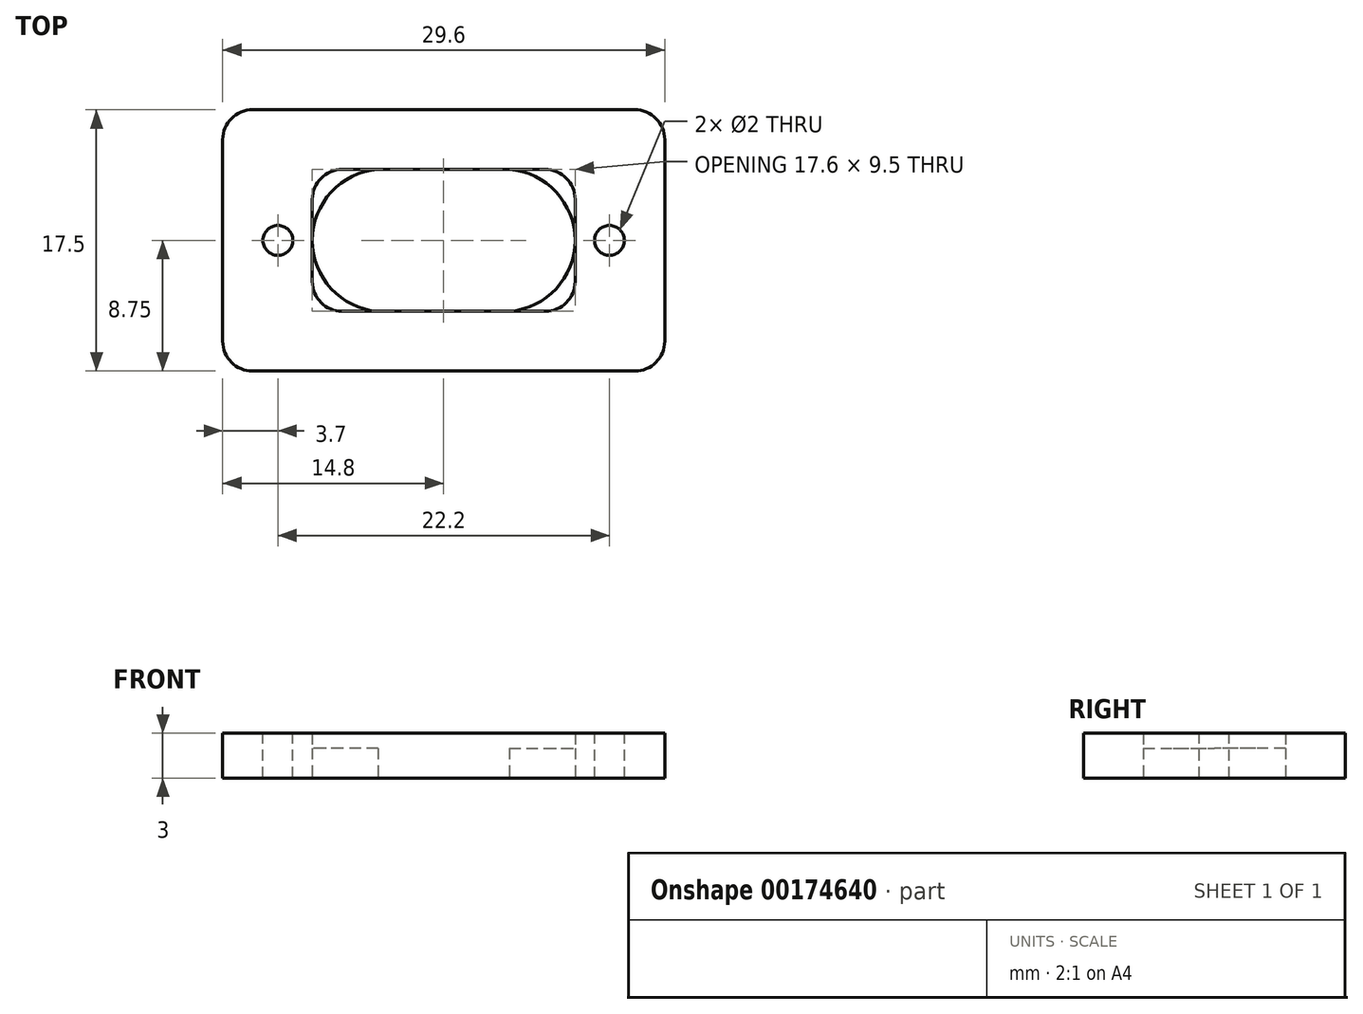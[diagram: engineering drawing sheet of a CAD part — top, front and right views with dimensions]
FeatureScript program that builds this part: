
annotation { "Feature Type Name" : "Feature", "Feature Type Description" : "" }
export const myFeature = defineFeature(function(context is Context, id is Id, definition is map)
    precondition{}
    {
        {
            var Q0;
            Q0=qCreatedBy(makeId("Top.planeOp"),FACE);
            var sketch = newSketch(context, id + "F0", { "sketchPlane" : qUnion([Q0])});
            skLineSegment(sketch, "E0", {"start": v(0, 4.75) * mm, "end": v(-8.8, 4.75) * mm});
            skLineSegment(sketch, "E1", {"start": v(-8.8, 4.75) * mm, "end": v(-8.8, 0) * mm});
            skLineSegment(sketch, "E2", {"start": v(-8.8, 0) * mm, "end": v(0, 0) * mm});
            skLineSegment(sketch, "E3", {"start": v(0, 0) * mm, "end": v(0, 4.75) * mm});
            skLineSegment(sketch, "E4", {"start": v(0, 4.75) * mm, "end": v(0, 8.75) * mm});
            skLineSegment(sketch, "E5", {"start": v(0, 8.75) * mm, "end": v(-14.8, 8.75) * mm});
            skLineSegment(sketch, "E6", {"start": v(-14.8, 8.75) * mm, "end": v(-14.8, 0) * mm});
            skLineSegment(sketch, "E7", {"start": v(-14.8, 0) * mm, "end": v(-8.8, 0) * mm});
            skPoint(sketch, "E8", {"position": v(-11.8, 0) * mm});
            skArc(sketch, "E9", {"start": v(-4.4, 4.75) * mm, "mid": v(-7.53, 3.24) * mm, "end": v(-8.8, 0) * mm});
            skSolve(sketch);
        }
        {
            var Q0;
            Q0=makeQuery(id+"F0.imprint","IMPRINT",FACE,{"disambiguationData":[TD([[makeQuery(id+"F0.imprint","IMPRINT",EDGE,{"derivedFrom":sQuery(id+"F0.wireOp",EDGE,"E0")}),-1.0]])]});
            extrude(context, id + "F1", {"entities" : qUnion([Q0]), "depth" : 3 * mm});
        }
        {
            var Q0;
            {var subQ1=sQuery(id+"F0.wireOp",EDGE,"E0");Q0=makeQuery(id+"F0.imprint","IMPRINT",FACE,{"disambiguationData":[TD([[makeQuery(id+"F0.imprint","IMPRINT",EDGE,{"derivedFrom":subQ1}),1.0]])]});}
            extrude(context, id + "F2", {"entities" : qUnion([Q0]), "operationType" : NewBodyOperationType.ADD, "depth" : 2 * mm});
        }
        {
            var Q0;
            Q0=makeQuery(id+"F2.opExtrude","SWEPT_EDGE",EDGE,{"disambiguationData":[OSD([sQuery(id+"F0.wireOp",EDGE,"qcPsBwBO-vwPQ-kIej-kDFl-4bRjYbtzWEV6"),sQuery(id+"F0.wireOp",EDGE,"uFsI8KWR-XaW8-EUl2-ddZK-JC7lbAuVXMJP")])]});
            var Q1;
            Q1=makeQuery(id+"F1.opExtrude","SWEPT_EDGE",EDGE,{"disambiguationData":[OSD([sQuery(id+"F0.wireOp",EDGE,"E5"),sQuery(id+"F0.wireOp",EDGE,"E6")])]});
            var Q2;
            Q2=makeQuery(id+"F1.opExtrude","SWEPT_EDGE",EDGE,{"disambiguationData":[OSD([sQuery(id+"F0.wireOp",EDGE,"E0"),sQuery(id+"F0.wireOp",EDGE,"E1")])]});
            fillet(context, id + "F3", {"entities" : qUnion([Q0, Q1, Q2]), "radius" : 2 * mm, "tangentPropagation" : true, "allowEdgeOverflow" : false});
        }
        {
            var Q0;
            Q0=makeQuery(id+"F1.opExtrude","SWEPT_BODY",BODY,{"disambiguationData":[OSD([sQuery(id+"F0.wireOp",EDGE,"E0"),sQuery(id+"F0.wireOp",EDGE,"E1"),sQuery(id+"F0.wireOp",EDGE,"E4"),sQuery(id+"F0.wireOp",EDGE,"E5"),sQuery(id+"F0.wireOp",EDGE,"E6"),sQuery(id+"F0.wireOp",EDGE,"E7")])]});
            var Q1;
            Q1=makeQuery(id+"F1.opExtrude","SWEPT_FACE",FACE,{"disambiguationData":[OSD([sQuery(id+"F0.wireOp",EDGE,"E7")])]});
            mirror(context, id + "F4", {"operationType" : NewBodyOperationType.ADD, "entities" : qUnion([Q0]), "mirrorPlane" : qUnion([Q1])});
        }
        {
            var Q0;
            {var subQ0=makeQuery(id+"F1.opExtrude","CAP_FACE",FACE,{"disambiguationData":[OSD([sQuery(id+"F0.wireOp",EDGE,"E0"),sQuery(id+"F0.wireOp",EDGE,"E1"),sQuery(id+"F0.wireOp",EDGE,"E4"),sQuery(id+"F0.wireOp",EDGE,"E5"),sQuery(id+"F0.wireOp",EDGE,"E6"),sQuery(id+"F0.wireOp",EDGE,"E7")])],"isStart":false});var subQ1=makeQuery(id+"F4.boolean.opBoolean","MERGE",FACE,{"derivedFrom":[subQ0,makeQuery(id+"F4.opPattern","COPY",FACE,{"derivedFrom":subQ0,"instanceName":"1"})]});Q0=makeQuery(id+"F7.boolean.opBoolean","MERGE",FACE,{"derivedFrom":[subQ1,makeQuery(id+"F7.opPattern","COPY",FACE,{"derivedFrom":subQ1,"instanceName":"1"})]});}
            var sketch = newSketch(context, id + "F5", { "sketchPlane" : qUnion([Q0])});
            skPoint(sketch, "E10", {"position": v(-11.1, 0) * mm});
            skPoint(sketch, "E10.positionSnap0", {"position": v(-14.8, 0) * mm});
            skSolve(sketch);
        }
        {
            var Q0;
            Q0=sQuery(id+"F5.wireOp",VERTEX,"E10");
            var Q1;
            Q1=makeQuery(id+"F1.opExtrude","SWEPT_BODY",BODY,{"disambiguationData":[OSD([sQuery(id+"F0.wireOp",EDGE,"E0"),sQuery(id+"F0.wireOp",EDGE,"E1"),sQuery(id+"F0.wireOp",EDGE,"E4"),sQuery(id+"F0.wireOp",EDGE,"E5"),sQuery(id+"F0.wireOp",EDGE,"E6"),sQuery(id+"F0.wireOp",EDGE,"E7")])]});
            hole(context, id + "F6", {"style" : HoleStyle.SIMPLE, "endStyle" : HoleEndStyle.THROUGH, "holeDiameter" : 2 * mm, "locations" : qUnion([Q0]), "scope" : qUnion([Q1]), "isTappedThrough" : true});
        }
        {
            var Q0;
            Q0=makeQuery(id+"F1.opExtrude","SWEPT_BODY",BODY,{"disambiguationData":[OSD([sQuery(id+"F0.wireOp",EDGE,"E0"),sQuery(id+"F0.wireOp",EDGE,"E1"),sQuery(id+"F0.wireOp",EDGE,"E4"),sQuery(id+"F0.wireOp",EDGE,"E5"),sQuery(id+"F0.wireOp",EDGE,"E6"),sQuery(id+"F0.wireOp",EDGE,"E7")])]});
            var Q1;
            Q1=makeQuery(id+"F1.opExtrude","SWEPT_FACE",FACE,{"disambiguationData":[OSD([sQuery(id+"F0.wireOp",EDGE,"E4")])]});
            mirror(context, id + "F7", {"operationType" : NewBodyOperationType.ADD, "entities" : qUnion([Q0]), "mirrorPlane" : qUnion([Q1])});
        }
    });
